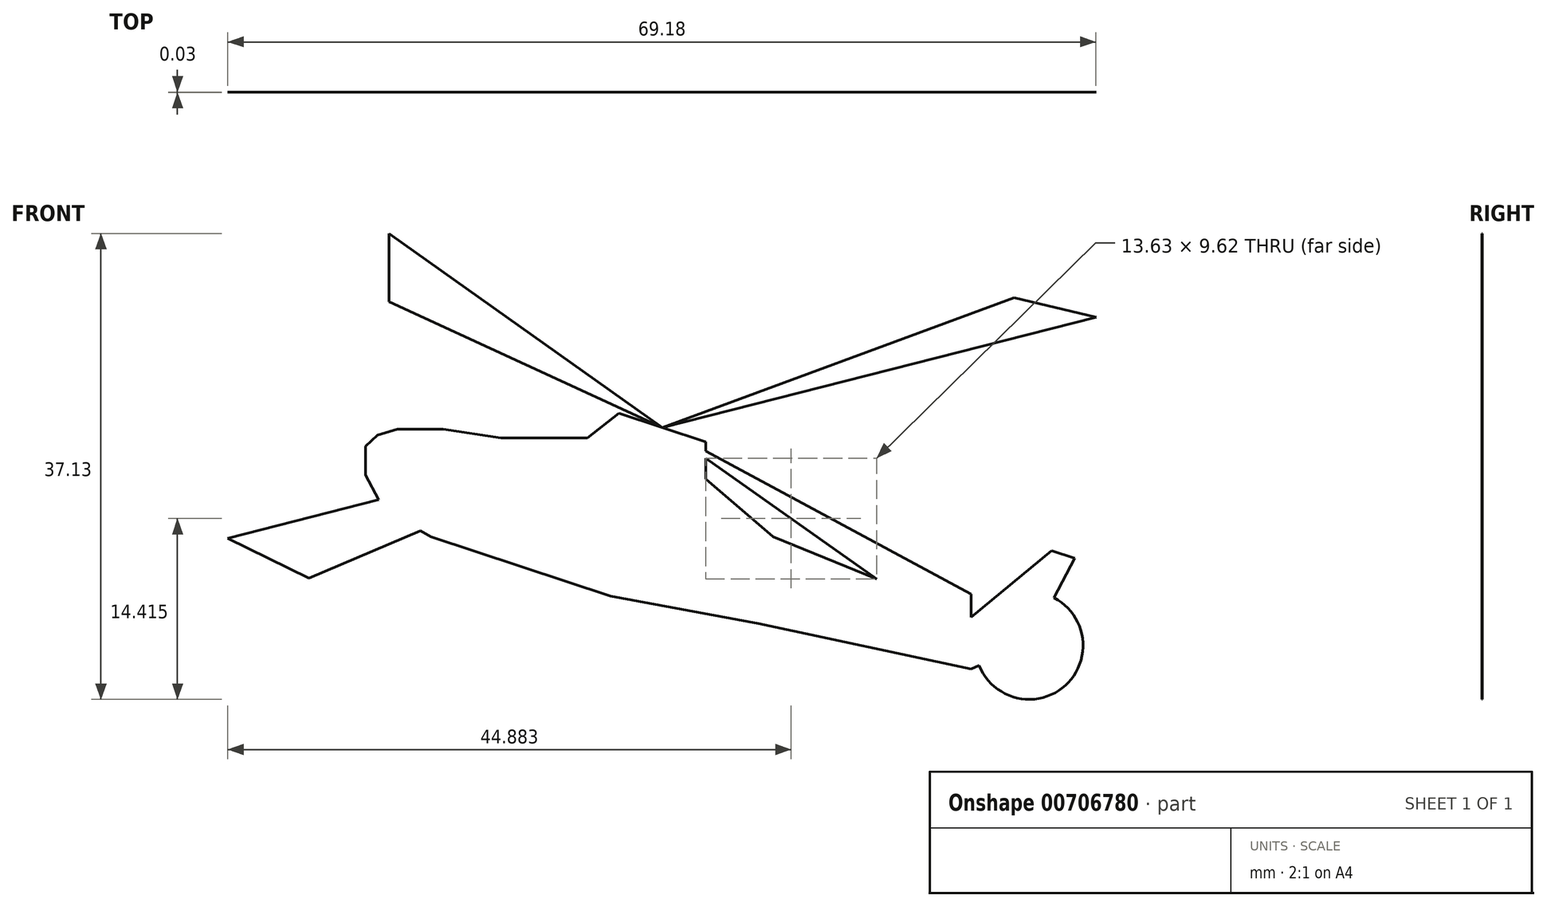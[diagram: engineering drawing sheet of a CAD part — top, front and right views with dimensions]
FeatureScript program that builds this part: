
annotation { "Feature Type Name" : "Feature", "Feature Type Description" : "" }
export const myFeature = defineFeature(function(context is Context, id is Id, definition is map)
    precondition{}
    {
        {
            var Q0;
            Q0=qCreatedBy(makeId("Front.planeOp"),FACE);
            var sketch = newSketch(context, id + "F0", { "sketchPlane" : qUnion([Q0])});
            skLineSegment(sketch, "E0", {"start": v(21.15, -6.97) * mm, "end": v(0, 0) * mm});
            skLineSegment(sketch, "E1", {"start": v(0, 0) * mm, "end": v(-27.1, 8.93) * mm});
            skLineSegment(sketch, "E2", {"start": v(-27.1, 8.93) * mm, "end": v(-27.1, 6.63) * mm});
            skLineSegment(sketch, "E3", {"start": v(-27.1, 6.63) * mm, "end": v(-25.7, 4) * mm});
            skLineSegment(sketch, "E4", {"start": v(-25.7, 4) * mm, "end": v(-21.9, 1.7) * mm});
            skLineSegment(sketch, "E5", {"start": v(-21.9, 1.7) * mm, "end": v(-7.58, -3.02) * mm});
            skLineSegment(sketch, "E6", {"start": v(-7.58, -3.02) * mm, "end": v(4.24, -5.21) * mm});
            skLineSegment(sketch, "E7", {"start": v(4.24, -5.21) * mm, "end": v(21.15, -8.83) * mm});
            skLineSegment(sketch, "E8", {"start": v(21.15, -8.83) * mm, "end": v(25.79, -6.97) * mm});
            skLineSegment(sketch, "E9", {"start": v(25.79, -6.97) * mm, "end": v(29.4, 0) * mm});
            skLineSegment(sketch, "E10", {"start": v(29.4, 0) * mm, "end": v(27.56, 0.6) * mm});
            skLineSegment(sketch, "E11", {"start": v(27.56, 0.6) * mm, "end": v(21.15, -4.72) * mm});
            skLineSegment(sketch, "E12", {"start": v(21.15, -4.72) * mm, "end": v(5.4, 1.7) * mm});
            skLineSegment(sketch, "E13", {"start": v(5.4, 1.7) * mm, "end": v(0, 6.3) * mm});
            skLineSegment(sketch, "E14", {"start": v(0, 6.3) * mm, "end": v(0, 9.26) * mm});
            skLineSegment(sketch, "E15", {"start": v(0, 9.26) * mm, "end": v(-6.9, 11.53) * mm});
            skLineSegment(sketch, "E16", {"start": v(-6.9, 11.53) * mm, "end": v(-9.4, 9.6) * mm});
            skLineSegment(sketch, "E17", {"start": v(-9.4, 9.6) * mm, "end": v(-16.32, 9.6) * mm});
            skLineSegment(sketch, "E18", {"start": v(-16.32, 9.6) * mm, "end": v(-20.9, 10.28) * mm});
            skLineSegment(sketch, "E19", {"start": v(-20.9, 10.28) * mm, "end": v(-24.55, 10.28) * mm});
            skLineSegment(sketch, "E20", {"start": v(-24.55, 10.28) * mm, "end": v(-26.14, 9.8) * mm});
            skLineSegment(sketch, "E21", {"start": v(-26.14, 9.8) * mm, "end": v(-27.1, 8.93) * mm});
            skPoint(sketch, "E22", {"position": v(-3.45, 10.4) * mm});
            skLineSegment(sketch, "E23", {"start": v(-3.45, 10.4) * mm, "end": v(31.11, 19.19) * mm});
            skLineSegment(sketch, "E24", {"start": v(-3.45, 10.4) * mm, "end": v(-38.07, 1.59) * mm});
            skLineSegment(sketch, "E25", {"start": v(-3.45, 10.4) * mm, "end": v(-25.24, 25.87) * mm});
            skLineSegment(sketch, "E26", {"start": v(-3.45, 10.4) * mm, "end": v(21.15, -6.97) * mm});
            skCircle(sketch, "E27", {"center": v(25.79, -6.97) * mm, "radius": 4.29 * mm});
            skLineSegment(sketch, "E28", {"start": v(-25.24, 25.87) * mm, "end": v(-25.24, 20.43) * mm});
            skLineSegment(sketch, "E29", {"start": v(-25.24, 20.43) * mm, "end": v(-3.45, 10.4) * mm});
            skLineSegment(sketch, "E30", {"start": v(-38.07, 1.59) * mm, "end": v(-31.6, -1.61) * mm});
            skLineSegment(sketch, "E31", {"start": v(-31.6, -1.61) * mm, "end": v(-3.45, 10.4) * mm});
            skLineSegment(sketch, "E32", {"start": v(21.15, -6.97) * mm, "end": v(21.15, -2.86) * mm});
            skLineSegment(sketch, "E33", {"start": v(21.15, -2.86) * mm, "end": v(-3.45, 10.4) * mm});
            skLineSegment(sketch, "E34", {"start": v(31.11, 19.19) * mm, "end": v(24.6, 20.74) * mm});
            skLineSegment(sketch, "E35", {"start": v(24.6, 20.74) * mm, "end": v(-3.45, 10.4) * mm});
            skSolve(sketch);
        }
        {
            var Q0;
            Q0 = qSketchRegion(id + "F0", true);
            extrude(context, id + "F1", {"entities" : qUnion([Q0]), "depth" : 0.03 * mm, "offsetDistance" : 25.4 * mm});
        }
    });
